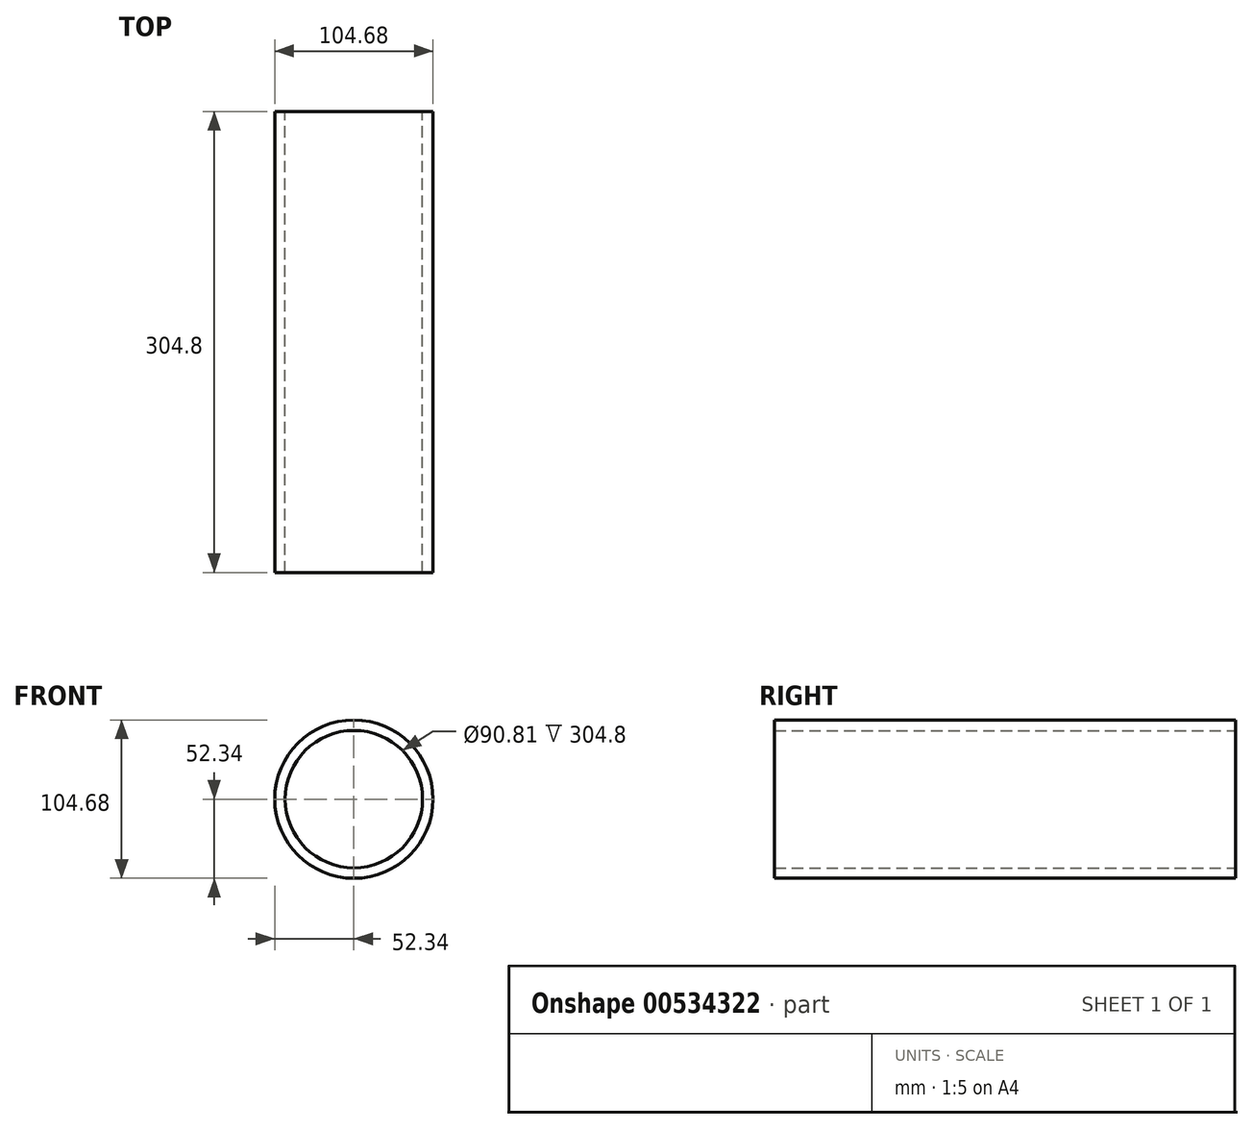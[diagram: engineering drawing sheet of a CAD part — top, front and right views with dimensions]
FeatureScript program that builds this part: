
annotation { "Feature Type Name" : "Feature", "Feature Type Description" : "" }
export const myFeature = defineFeature(function(context is Context, id is Id, definition is map)
    precondition{}
    {
        {
            var Q0;
            Q0=qCreatedBy(makeId("Front.planeOp"),FACE);
            var sketch = newSketch(context, id + "F0", { "sketchPlane" : qUnion([Q0])});
            skCircle(sketch, "E0", {"center": v(0, 0) * mm, "radius": 11.88 * mm});
            skCircle(sketch, "E1", {"center": v(0, -11.88) * mm, "radius": 11.88 * mm});
            skCircle(sketch, "E2", {"center": v(0, 0) * mm, "radius": 52.34 * mm});
            skCircle(sketch, "E3", {"center": v(0, 0) * mm, "radius": 45.4 * mm});
            skSolve(sketch);
        }
        {
            var Q0;
            Q0 = qSketchRegion(id + "F0", true);
            extrude(context, id + "F1", {"entities" : qUnion([Q0]), "depth" : 304.8 * mm, "offsetDistance" : 25.4 * mm});
        }
    });
